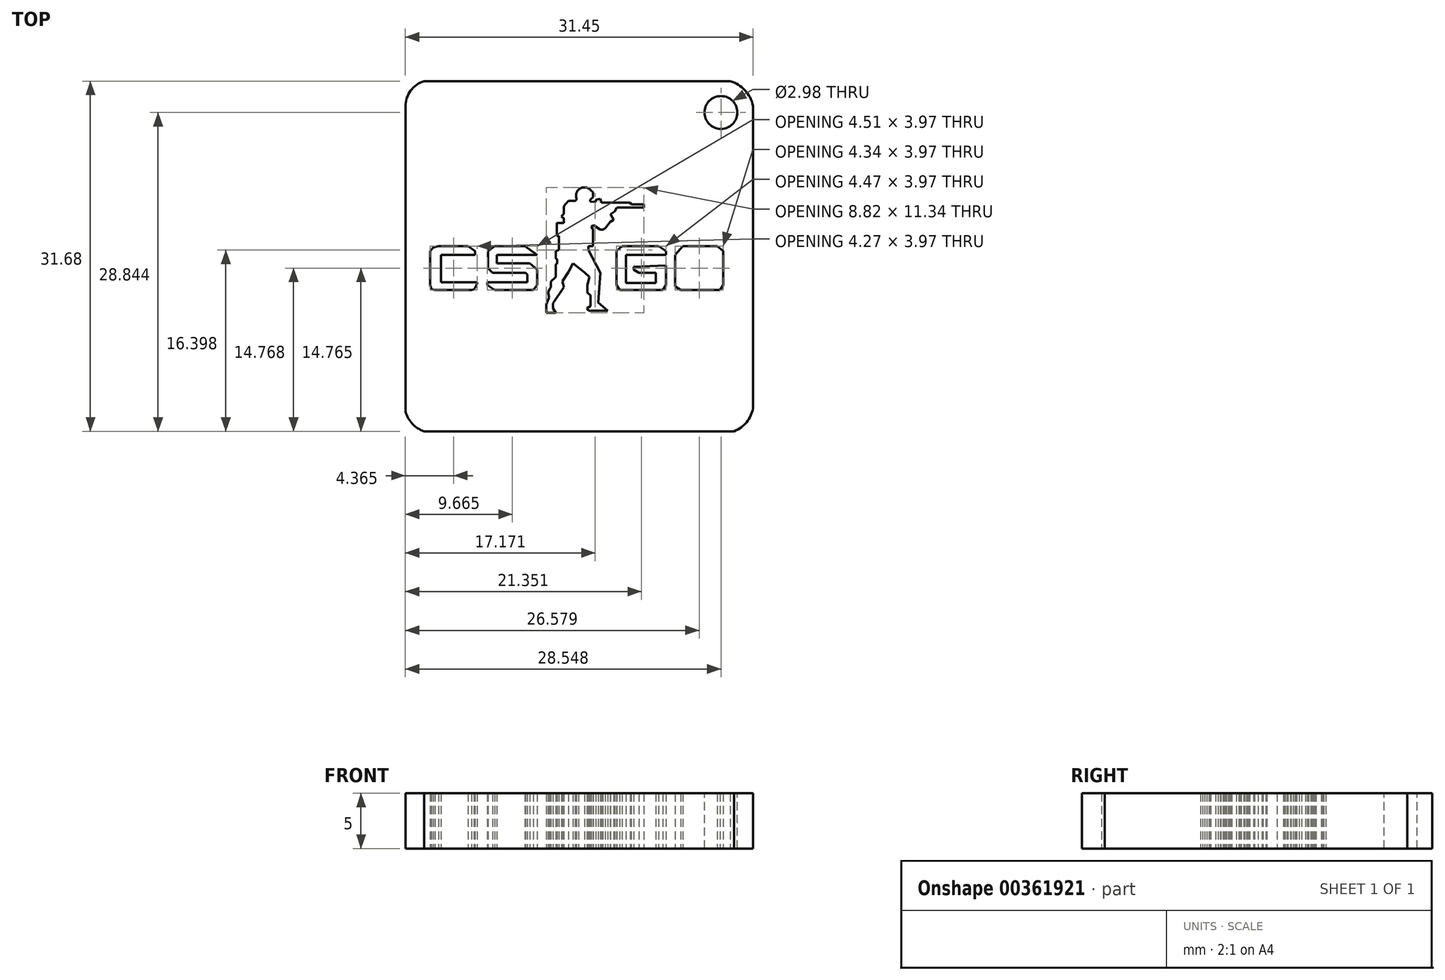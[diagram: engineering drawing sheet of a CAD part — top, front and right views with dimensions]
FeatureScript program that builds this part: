
annotation { "Feature Type Name" : "Feature", "Feature Type Description" : "" }
export const myFeature = defineFeature(function(context is Context, id is Id, definition is map)
    precondition{}
    {
        {
            var Q0;
            Q0=qCreatedBy(makeId("Top.planeOp"),FACE);
            var sketch = newSketch(context, id + "F0", { "sketchPlane" : qUnion([Q0])});
            skLineSegment(sketch, "E0", {"start": v(-16.2, 13.42) * mm, "end": v(-16.2, -14.16) * mm});
            skArc(sketch, "E1", {"start": v(-16.2, -14.16) * mm, "mid": v(-15.58, -15.27) * mm, "end": v(-14.52, -15.96) * mm});
            skLineSegment(sketch, "E2", {"start": v(-14.52, -15.96) * mm, "end": v(13.54, -15.96) * mm});
            skArc(sketch, "E3", {"start": v(13.54, -15.96) * mm, "mid": v(14.66, -15.14) * mm, "end": v(15.25, -13.88) * mm});
            skLineSegment(sketch, "E4", {"start": v(15.25, -13.88) * mm, "end": v(15.25, 13.5) * mm});
            skArc(sketch, "E5", {"start": v(15.25, 13.5) * mm, "mid": v(14.53, 14.89) * mm, "end": v(13.2, 15.72) * mm});
            skLineSegment(sketch, "E6", {"start": v(13.2, 15.72) * mm, "end": v(-14.5, 15.72) * mm});
            skArc(sketch, "E7", {"start": v(-14.5, 15.72) * mm, "mid": v(-15.73, 14.85) * mm, "end": v(-16.2, 13.42) * mm});
            skLineSegment(sketch, "E8", {"start": v(-12.75, 0) * mm, "end": v(-9.89, 0) * mm});
            skLineSegment(sketch, "E9", {"start": v(-9.89, 0) * mm, "end": v(-9.89, 0.36) * mm});
            skLineSegment(sketch, "E10", {"start": v(-9.89, 0.36) * mm, "end": v(-10.53, 0.8) * mm});
            skLineSegment(sketch, "E11", {"start": v(-10.53, 0.8) * mm, "end": v(-13.2, 0.8) * mm});
            skLineSegment(sketch, "E12", {"start": v(-13.2, 0.8) * mm, "end": v(-13.66, 0.67) * mm});
            skLineSegment(sketch, "E13", {"start": v(-13.66, 0.67) * mm, "end": v(-13.97, 0.36) * mm});
            skLineSegment(sketch, "E14", {"start": v(-13.97, 0.36) * mm, "end": v(-13.97, -2.73) * mm});
            skLineSegment(sketch, "E15", {"start": v(-13.97, -2.73) * mm, "end": v(-13.82, -3.11) * mm});
            skLineSegment(sketch, "E16", {"start": v(-13.82, -3.11) * mm, "end": v(-13.52, -3.18) * mm});
            skLineSegment(sketch, "E17", {"start": v(-13.52, -3.18) * mm, "end": v(-10.21, -3.18) * mm});
            skLineSegment(sketch, "E18", {"start": v(-10.21, -3.18) * mm, "end": v(-9.99, -3.11) * mm});
            skLineSegment(sketch, "E19", {"start": v(-9.99, -3.11) * mm, "end": v(-9.89, -3) * mm});
            skLineSegment(sketch, "E20", {"start": v(-9.89, -3) * mm, "end": v(-9.7, -2.6) * mm});
            skLineSegment(sketch, "E21", {"start": v(-9.7, -2.6) * mm, "end": v(-9.7, -2.47) * mm});
            skLineSegment(sketch, "E22", {"start": v(-9.7, -2.47) * mm, "end": v(-12.97, -2.47) * mm});
            skLineSegment(sketch, "E23", {"start": v(-12.97, -2.47) * mm, "end": v(-12.97, -0.32) * mm});
            skLineSegment(sketch, "E24", {"start": v(-12.97, -0.32) * mm, "end": v(-12.97, 0) * mm});
            skLineSegment(sketch, "E25", {"start": v(-12.97, 0) * mm, "end": v(-12.75, 0) * mm});
            skLineSegment(sketch, "E26", {"start": v(-8.11, 0.8) * mm, "end": v(-5.38, 0.8) * mm});
            skLineSegment(sketch, "E27", {"start": v(-5.38, 0.8) * mm, "end": v(-4.28, 0) * mm});
            skLineSegment(sketch, "E28", {"start": v(-4.28, 0) * mm, "end": v(-7.92, 0) * mm});
            skLineSegment(sketch, "E29", {"start": v(-7.92, 0) * mm, "end": v(-7.92, -0.77) * mm});
            skLineSegment(sketch, "E30", {"start": v(-7.92, -0.77) * mm, "end": v(-4.94, -0.77) * mm});
            skLineSegment(sketch, "E31", {"start": v(-4.94, -0.77) * mm, "end": v(-4.28, -1.33) * mm});
            skLineSegment(sketch, "E32", {"start": v(-4.28, -1.33) * mm, "end": v(-4.28, -2.73) * mm});
            skLineSegment(sketch, "E33", {"start": v(-4.28, -2.73) * mm, "end": v(-4.61, -3.18) * mm});
            skLineSegment(sketch, "E34", {"start": v(-4.61, -3.18) * mm, "end": v(-8.13, -3.18) * mm});
            skLineSegment(sketch, "E35", {"start": v(-8.13, -3.18) * mm, "end": v(-8.79, -2.73) * mm});
            skLineSegment(sketch, "E36", {"start": v(-8.79, -2.73) * mm, "end": v(-8.79, -2.47) * mm});
            skLineSegment(sketch, "E37", {"start": v(-8.79, -2.47) * mm, "end": v(-5.15, -2.47) * mm});
            skLineSegment(sketch, "E38", {"start": v(-5.15, -2.47) * mm, "end": v(-5.15, -1.76) * mm});
            skLineSegment(sketch, "E39", {"start": v(-5.15, -1.76) * mm, "end": v(-5.32, -1.6) * mm});
            skLineSegment(sketch, "E40", {"start": v(-5.32, -1.6) * mm, "end": v(-8.3, -1.6) * mm});
            skLineSegment(sketch, "E41", {"start": v(-8.3, -1.6) * mm, "end": v(-8.72, -1.2) * mm});
            skLineSegment(sketch, "E42", {"start": v(-8.72, -1.2) * mm, "end": v(-8.72, 0) * mm});
            skLineSegment(sketch, "E43", {"start": v(-8.72, 0) * mm, "end": v(-8.72, 0.36) * mm});
            skLineSegment(sketch, "E44", {"start": v(-8.72, 0.36) * mm, "end": v(-8.11, 0.8) * mm});
            skLineSegment(sketch, "E45", {"start": v(0.51, 4.82) * mm, "end": v(0.51, 5) * mm});
            skLineSegment(sketch, "E46", {"start": v(0.63, 5.08) * mm, "end": v(0.51, 5) * mm});
            skLineSegment(sketch, "E47", {"start": v(0.63, 5.08) * mm, "end": v(0.77, 5.21) * mm});
            skLineSegment(sketch, "E48", {"start": v(0.77, 5.21) * mm, "end": v(0.77, 5.36) * mm});
            skLineSegment(sketch, "E49", {"start": v(0.77, 5.36) * mm, "end": v(0.77, 5.53) * mm});
            skLineSegment(sketch, "E50", {"start": v(0.77, 5.53) * mm, "end": v(0.77, 5.7) * mm});
            skLineSegment(sketch, "E51", {"start": v(0.77, 5.7) * mm, "end": v(0.63, 5.81) * mm});
            skLineSegment(sketch, "E52", {"start": v(0.63, 5.81) * mm, "end": v(0.51, 5.91) * mm});
            skArc(sketch, "E53", {"start": v(0.51, 5.91) * mm, "mid": v(-0.01, 6.1) * mm, "end": v(-0.53, 5.91) * mm});
            skArc(sketch, "E54", {"start": v(-0.53, 5.91) * mm, "mid": v(-0.75, 5.53) * mm, "end": v(-0.71, 5.1) * mm});
            skArc(sketch, "E55", {"start": v(-0.84, 4.9) * mm, "mid": v(-0.74, 4.97) * mm, "end": v(-0.71, 5.1) * mm});
            skLineSegment(sketch, "E56", {"start": v(-0.84, 4.9) * mm, "end": v(-1.45, 4.9) * mm});
            skLineSegment(sketch, "E57", {"start": v(-1.45, 4.9) * mm, "end": v(-1.86, 4.42) * mm});
            skLineSegment(sketch, "E58", {"start": v(-1.86, 4.42) * mm, "end": v(-1.86, 3.7) * mm});
            skLineSegment(sketch, "E59", {"start": v(-1.86, 3.7) * mm, "end": v(-2.1, 3.5) * mm});
            skLineSegment(sketch, "E60", {"start": v(-2.1, 3.5) * mm, "end": v(-2, 3.39) * mm});
            skLineSegment(sketch, "E61", {"start": v(-2, 3.39) * mm, "end": v(-1.86, 3.32) * mm});
            skLineSegment(sketch, "E62", {"start": v(-1.86, 3.32) * mm, "end": v(-1.86, 2.9) * mm});
            skLineSegment(sketch, "E63", {"start": v(-1.86, 2.9) * mm, "end": v(-2.5, 2.9) * mm});
            skLineSegment(sketch, "E64", {"start": v(-2.5, 2.9) * mm, "end": v(-2.5, 1.71) * mm});
            skLineSegment(sketch, "E65", {"start": v(-2.5, 1.71) * mm, "end": v(-2.3, 1.71) * mm});
            skLineSegment(sketch, "E66", {"start": v(-2.3, 1.71) * mm, "end": v(-2.3, 0.43) * mm});
            skLineSegment(sketch, "E67", {"start": v(-2.3, 0.43) * mm, "end": v(-2.6, 0.34) * mm});
            skLineSegment(sketch, "E68", {"start": v(-2.6, 0.34) * mm, "end": v(-2.6, -0.32) * mm});
            skLineSegment(sketch, "E69", {"start": v(-2.6, -0.32) * mm, "end": v(-2.46, -0.42) * mm});
            skLineSegment(sketch, "E70", {"start": v(-2.46, -0.42) * mm, "end": v(-2.46, -0.77) * mm});
            skLineSegment(sketch, "E71", {"start": v(-2.46, -0.77) * mm, "end": v(-2.6, -0.87) * mm});
            skLineSegment(sketch, "E72", {"start": v(-2.6, -0.87) * mm, "end": v(-2.6, -2) * mm});
            skLineSegment(sketch, "E73", {"start": v(-2.6, -2) * mm, "end": v(-3.03, -2.4) * mm});
            skLineSegment(sketch, "E74", {"start": v(-3.03, -2.4) * mm, "end": v(-3.03, -2.88) * mm});
            skLineSegment(sketch, "E75", {"start": v(-3.03, -2.88) * mm, "end": v(-3.14, -3.07) * mm});
            skLineSegment(sketch, "E76", {"start": v(-3.14, -3.07) * mm, "end": v(-3.3, -3.37) * mm});
            skLineSegment(sketch, "E77", {"start": v(-3.3, -3.37) * mm, "end": v(-3.2, -3.84) * mm});
            skLineSegment(sketch, "E78", {"start": v(-3.2, -3.84) * mm, "end": v(-3.44, -4.47) * mm});
            skLineSegment(sketch, "E79", {"start": v(-3.44, -4.47) * mm, "end": v(-3.44, -4.87) * mm});
            skLineSegment(sketch, "E80", {"start": v(-3.44, -4.87) * mm, "end": v(-3.44, -5.23) * mm});
            skLineSegment(sketch, "E81", {"start": v(-3.44, -5.23) * mm, "end": v(-2.6, -5.23) * mm});
            skLineSegment(sketch, "E82", {"start": v(-2.6, -5.23) * mm, "end": v(-2.85, -4.83) * mm});
            skLineSegment(sketch, "E83", {"start": v(-2.85, -4.83) * mm, "end": v(-2.85, -4.38) * mm});
            skLineSegment(sketch, "E84", {"start": v(-2.85, -4.38) * mm, "end": v(-1.86, -2.91) * mm});
            skLineSegment(sketch, "E85", {"start": v(-1.86, -2.91) * mm, "end": v(-2, -2.39) * mm});
            skLineSegment(sketch, "E86", {"start": v(-2, -2.39) * mm, "end": v(-1.45, -1.55) * mm});
            skLineSegment(sketch, "E87", {"start": v(-1.45, -1.55) * mm, "end": v(-1.03, -0.77) * mm});
            skLineSegment(sketch, "E88", {"start": v(-1.03, -0.77) * mm, "end": v(0, -1.59) * mm});
            skLineSegment(sketch, "E89", {"start": v(0, -1.59) * mm, "end": v(0.46, -2) * mm});
            skLineSegment(sketch, "E90", {"start": v(0.46, -2) * mm, "end": v(0.27, -2.73) * mm});
            skLineSegment(sketch, "E91", {"start": v(0.27, -2.73) * mm, "end": v(0.27, -3.44) * mm});
            skLineSegment(sketch, "E92", {"start": v(0.27, -3.44) * mm, "end": v(0.54, -3.64) * mm});
            skLineSegment(sketch, "E93", {"start": v(0.54, -3.64) * mm, "end": v(0.54, -4.65) * mm});
            skLineSegment(sketch, "E94", {"start": v(0.54, -4.65) * mm, "end": v(0.24, -4.83) * mm});
            skLineSegment(sketch, "E95", {"start": v(0.24, -4.83) * mm, "end": v(0.37, -5.04) * mm});
            skLineSegment(sketch, "E96", {"start": v(0.37, -5.04) * mm, "end": v(2.12, -5.04) * mm});
            skLineSegment(sketch, "E97", {"start": v(2.12, -5.04) * mm, "end": v(1.23, -4.3) * mm});
            skLineSegment(sketch, "E98", {"start": v(1.23, -4.3) * mm, "end": v(1.44, -1.63) * mm});
            skLineSegment(sketch, "E99", {"start": v(1.44, -1.63) * mm, "end": v(0.35, 0.43) * mm});
            skLineSegment(sketch, "E100", {"start": v(0.35, 0.43) * mm, "end": v(0.35, 0.8) * mm});
            skLineSegment(sketch, "E101", {"start": v(0.35, 0.8) * mm, "end": v(0.78, 0.8) * mm});
            skLineSegment(sketch, "E102", {"start": v(0.78, 0.8) * mm, "end": v(0.78, 2.32) * mm});
            skLineSegment(sketch, "E103", {"start": v(0.78, 2.32) * mm, "end": v(0.63, 2.58) * mm});
            skLineSegment(sketch, "E104", {"start": v(0.63, 2.58) * mm, "end": v(0.81, 2.7) * mm});
            skLineSegment(sketch, "E105", {"start": v(0.81, 2.7) * mm, "end": v(1.44, 2.28) * mm});
            skLineSegment(sketch, "E106", {"start": v(1.44, 2.28) * mm, "end": v(1.65, 2.28) * mm});
            skLineSegment(sketch, "E107", {"start": v(1.65, 2.28) * mm, "end": v(1.88, 2.42) * mm});
            skLineSegment(sketch, "E108", {"start": v(1.88, 2.42) * mm, "end": v(2.33, 2.98) * mm});
            skLineSegment(sketch, "E109", {"start": v(2.33, 2.98) * mm, "end": v(2.5, 3.08) * mm});
            skLineSegment(sketch, "E110", {"start": v(2.5, 3.08) * mm, "end": v(2.66, 3.18) * mm});
            skLineSegment(sketch, "E111", {"start": v(2.66, 3.18) * mm, "end": v(2.56, 3.34) * mm});
            skLineSegment(sketch, "E112", {"start": v(2.56, 3.34) * mm, "end": v(2.35, 3.7) * mm});
            skLineSegment(sketch, "E113", {"start": v(2.35, 3.7) * mm, "end": v(2.74, 3.94) * mm});
            skLineSegment(sketch, "E114", {"start": v(2.74, 3.94) * mm, "end": v(2.94, 4.27) * mm});
            skLineSegment(sketch, "E115", {"start": v(2.94, 4.27) * mm, "end": v(4.28, 4.27) * mm});
            skLineSegment(sketch, "E116", {"start": v(4.28, 4.27) * mm, "end": v(5.38, 4.27) * mm});
            skLineSegment(sketch, "E117", {"start": v(5.38, 4.27) * mm, "end": v(5.38, 4.57) * mm});
            skLineSegment(sketch, "E118", {"start": v(5.38, 4.57) * mm, "end": v(4.24, 4.57) * mm});
            skLineSegment(sketch, "E119", {"start": v(4.24, 4.57) * mm, "end": v(4.14, 4.74) * mm});
            skLineSegment(sketch, "E120", {"start": v(4.14, 4.74) * mm, "end": v(1.55, 4.74) * mm});
            skLineSegment(sketch, "E121", {"start": v(1.55, 4.74) * mm, "end": v(1.44, 5.1) * mm});
            skLineSegment(sketch, "E122", {"start": v(1.44, 5.1) * mm, "end": v(1.03, 4.97) * mm});
            skLineSegment(sketch, "E123", {"start": v(1.03, 4.97) * mm, "end": v(1.03, 4.78) * mm});
            skLineSegment(sketch, "E124", {"start": v(1.03, 4.78) * mm, "end": v(0.51, 4.82) * mm});
            skLineSegment(sketch, "E125", {"start": v(1.82, 4.1) * mm, "end": v(1.68, 3.83) * mm});
            skLineSegment(sketch, "E126", {"start": v(1.68, 3.83) * mm, "end": v(1.44, 3.77) * mm});
            skLineSegment(sketch, "E127", {"start": v(1.44, 3.77) * mm, "end": v(1.52, 3.63) * mm});
            skLineSegment(sketch, "E128", {"start": v(1.52, 3.63) * mm, "end": v(1.8, 3.63) * mm});
            skLineSegment(sketch, "E129", {"start": v(1.8, 3.63) * mm, "end": v(1.82, 4.1) * mm});
            skLineSegment(sketch, "E130", {"start": v(4.46, -1.07) * mm, "end": v(4.46, -1.33) * mm});
            skLineSegment(sketch, "E131", {"start": v(4.46, -1.33) * mm, "end": v(4.94, -1.63) * mm});
            skLineSegment(sketch, "E132", {"start": v(4.94, -1.63) * mm, "end": v(6.45, -1.63) * mm});
            skLineSegment(sketch, "E133", {"start": v(6.45, -1.63) * mm, "end": v(6.45, -2.53) * mm});
            skLineSegment(sketch, "E134", {"start": v(6.45, -2.53) * mm, "end": v(3.77, -2.53) * mm});
            skLineSegment(sketch, "E135", {"start": v(3.77, -2.53) * mm, "end": v(3.77, 0) * mm});
            skLineSegment(sketch, "E136", {"start": v(3.77, 0) * mm, "end": v(7.39, 0) * mm});
            skLineSegment(sketch, "E137", {"start": v(7.39, 0) * mm, "end": v(7.39, 0.34) * mm});
            skLineSegment(sketch, "E138", {"start": v(7.39, 0.34) * mm, "end": v(6.7, 0.8) * mm});
            skLineSegment(sketch, "E139", {"start": v(6.7, 0.8) * mm, "end": v(3.42, 0.8) * mm});
            skLineSegment(sketch, "E140", {"start": v(3.42, 0.8) * mm, "end": v(2.91, 0.34) * mm});
            skLineSegment(sketch, "E141", {"start": v(2.91, 0.34) * mm, "end": v(2.91, -2.73) * mm});
            skLineSegment(sketch, "E142", {"start": v(2.91, -2.73) * mm, "end": v(3.19, -3.18) * mm});
            skLineSegment(sketch, "E143", {"start": v(3.19, -3.18) * mm, "end": v(7.08, -3.18) * mm});
            skLineSegment(sketch, "E144", {"start": v(7.08, -3.18) * mm, "end": v(7.36, -2.73) * mm});
            skLineSegment(sketch, "E145", {"start": v(7.36, -2.73) * mm, "end": v(7.36, -0.97) * mm});
            skLineSegment(sketch, "E146", {"start": v(7.36, -0.97) * mm, "end": v(4.46, -1.07) * mm});
            skLineSegment(sketch, "E147", {"start": v(12, 0.8) * mm, "end": v(8.9, 0.8) * mm});
            skLineSegment(sketch, "E148", {"start": v(8.9, 0.8) * mm, "end": v(8.2, 0) * mm});
            skLineSegment(sketch, "E149", {"start": v(8.2, 0) * mm, "end": v(8.2, -2.86) * mm});
            skLineSegment(sketch, "E150", {"start": v(8.2, -2.86) * mm, "end": v(8.7, -3.18) * mm});
            skLineSegment(sketch, "E151", {"start": v(8.7, -3.18) * mm, "end": v(12.26, -3.18) * mm});
            skLineSegment(sketch, "E152", {"start": v(12.26, -3.18) * mm, "end": v(12.55, -2.73) * mm});
            skLineSegment(sketch, "E153", {"start": v(12.55, -2.73) * mm, "end": v(12.55, 0.34) * mm});
            skLineSegment(sketch, "E154", {"start": v(12.55, 0.34) * mm, "end": v(12, 0.8) * mm});
            skLineSegment(sketch, "E155", {"start": v(9.15, 0) * mm, "end": v(11.72, 0) * mm});
            skLineSegment(sketch, "E156", {"start": v(11.72, 0) * mm, "end": v(11.72, -2.57) * mm});
            skLineSegment(sketch, "E157", {"start": v(11.72, -2.57) * mm, "end": v(9.15, -2.57) * mm});
            skLineSegment(sketch, "E158", {"start": v(9.15, -2.57) * mm, "end": v(9.15, 0) * mm});
            skSolve(sketch);
        }
        {
            var Q0;
            Q0 = qSketchRegion(id + "F0", true);
            extrude(context, id + "F1", {"entities" : qUnion([Q0]), "depth" : 5 * mm});
        }
        {
            var Q0;
            Q0=makeQuery(id+"F1.opExtrude","CAP_FACE",FACE,{"disambiguationData":[OSD([sQuery(id+"F0.wireOp",EDGE,"E0"),sQuery(id+"F0.wireOp",EDGE,"E1"),sQuery(id+"F0.wireOp",EDGE,"E2"),sQuery(id+"F0.wireOp",EDGE,"E3"),sQuery(id+"F0.wireOp",EDGE,"E4"),sQuery(id+"F0.wireOp",EDGE,"E5"),sQuery(id+"F0.wireOp",EDGE,"E6"),sQuery(id+"F0.wireOp",EDGE,"E7"),sQuery(id+"F0.wireOp",EDGE,"E8"),sQuery(id+"F0.wireOp",EDGE,"E9"),sQuery(id+"F0.wireOp",EDGE,"E10"),sQuery(id+"F0.wireOp",EDGE,"E11"),sQuery(id+"F0.wireOp",EDGE,"E12"),sQuery(id+"F0.wireOp",EDGE,"E13"),sQuery(id+"F0.wireOp",EDGE,"E14"),sQuery(id+"F0.wireOp",EDGE,"E15"),sQuery(id+"F0.wireOp",EDGE,"E16"),sQuery(id+"F0.wireOp",EDGE,"E17"),sQuery(id+"F0.wireOp",EDGE,"E18"),sQuery(id+"F0.wireOp",EDGE,"E19"),sQuery(id+"F0.wireOp",EDGE,"E20"),sQuery(id+"F0.wireOp",EDGE,"E21"),sQuery(id+"F0.wireOp",EDGE,"E22"),sQuery(id+"F0.wireOp",EDGE,"E23"),sQuery(id+"F0.wireOp",EDGE,"E24"),sQuery(id+"F0.wireOp",EDGE,"E25"),sQuery(id+"F0.wireOp",EDGE,"E26"),sQuery(id+"F0.wireOp",EDGE,"E27"),sQuery(id+"F0.wireOp",EDGE,"E28"),sQuery(id+"F0.wireOp",EDGE,"E29"),sQuery(id+"F0.wireOp",EDGE,"E30"),sQuery(id+"F0.wireOp",EDGE,"E31"),sQuery(id+"F0.wireOp",EDGE,"E32"),sQuery(id+"F0.wireOp",EDGE,"E33"),sQuery(id+"F0.wireOp",EDGE,"E34"),sQuery(id+"F0.wireOp",EDGE,"E35"),sQuery(id+"F0.wireOp",EDGE,"E36"),sQuery(id+"F0.wireOp",EDGE,"E37"),sQuery(id+"F0.wireOp",EDGE,"E38"),sQuery(id+"F0.wireOp",EDGE,"E39"),sQuery(id+"F0.wireOp",EDGE,"E40"),sQuery(id+"F0.wireOp",EDGE,"E41"),sQuery(id+"F0.wireOp",EDGE,"E42"),sQuery(id+"F0.wireOp",EDGE,"E43"),sQuery(id+"F0.wireOp",EDGE,"E44"),sQuery(id+"F0.wireOp",EDGE,"E45"),sQuery(id+"F0.wireOp",EDGE,"E46"),sQuery(id+"F0.wireOp",EDGE,"E47"),sQuery(id+"F0.wireOp",EDGE,"E48"),sQuery(id+"F0.wireOp",EDGE,"E49"),sQuery(id+"F0.wireOp",EDGE,"E50"),sQuery(id+"F0.wireOp",EDGE,"E51"),sQuery(id+"F0.wireOp",EDGE,"E52"),sQuery(id+"F0.wireOp",EDGE,"E53"),sQuery(id+"F0.wireOp",EDGE,"E54"),sQuery(id+"F0.wireOp",EDGE,"E55"),sQuery(id+"F0.wireOp",EDGE,"E56"),sQuery(id+"F0.wireOp",EDGE,"E57"),sQuery(id+"F0.wireOp",EDGE,"E58"),sQuery(id+"F0.wireOp",EDGE,"E59"),sQuery(id+"F0.wireOp",EDGE,"E60"),sQuery(id+"F0.wireOp",EDGE,"E61"),sQuery(id+"F0.wireOp",EDGE,"E62"),sQuery(id+"F0.wireOp",EDGE,"E63"),sQuery(id+"F0.wireOp",EDGE,"E64"),sQuery(id+"F0.wireOp",EDGE,"E65"),sQuery(id+"F0.wireOp",EDGE,"E66"),sQuery(id+"F0.wireOp",EDGE,"E67"),sQuery(id+"F0.wireOp",EDGE,"E68"),sQuery(id+"F0.wireOp",EDGE,"E69"),sQuery(id+"F0.wireOp",EDGE,"E70"),sQuery(id+"F0.wireOp",EDGE,"E71"),sQuery(id+"F0.wireOp",EDGE,"E72"),sQuery(id+"F0.wireOp",EDGE,"E73"),sQuery(id+"F0.wireOp",EDGE,"E74"),sQuery(id+"F0.wireOp",EDGE,"E75"),sQuery(id+"F0.wireOp",EDGE,"E76"),sQuery(id+"F0.wireOp",EDGE,"E77"),sQuery(id+"F0.wireOp",EDGE,"E78"),sQuery(id+"F0.wireOp",EDGE,"E79"),sQuery(id+"F0.wireOp",EDGE,"E80"),sQuery(id+"F0.wireOp",EDGE,"E81"),sQuery(id+"F0.wireOp",EDGE,"E82"),sQuery(id+"F0.wireOp",EDGE,"E83"),sQuery(id+"F0.wireOp",EDGE,"E84"),sQuery(id+"F0.wireOp",EDGE,"E85"),sQuery(id+"F0.wireOp",EDGE,"E86"),sQuery(id+"F0.wireOp",EDGE,"E87"),sQuery(id+"F0.wireOp",EDGE,"E88"),sQuery(id+"F0.wireOp",EDGE,"E89"),sQuery(id+"F0.wireOp",EDGE,"E90"),sQuery(id+"F0.wireOp",EDGE,"E91"),sQuery(id+"F0.wireOp",EDGE,"E92"),sQuery(id+"F0.wireOp",EDGE,"E93"),sQuery(id+"F0.wireOp",EDGE,"E94"),sQuery(id+"F0.wireOp",EDGE,"E95"),sQuery(id+"F0.wireOp",EDGE,"E96"),sQuery(id+"F0.wireOp",EDGE,"E97"),sQuery(id+"F0.wireOp",EDGE,"E98"),sQuery(id+"F0.wireOp",EDGE,"E99"),sQuery(id+"F0.wireOp",EDGE,"E100"),sQuery(id+"F0.wireOp",EDGE,"E101"),sQuery(id+"F0.wireOp",EDGE,"E102"),sQuery(id+"F0.wireOp",EDGE,"E103"),sQuery(id+"F0.wireOp",EDGE,"E104"),sQuery(id+"F0.wireOp",EDGE,"E105"),sQuery(id+"F0.wireOp",EDGE,"E106"),sQuery(id+"F0.wireOp",EDGE,"E107"),sQuery(id+"F0.wireOp",EDGE,"E108"),sQuery(id+"F0.wireOp",EDGE,"E109"),sQuery(id+"F0.wireOp",EDGE,"E110"),sQuery(id+"F0.wireOp",EDGE,"E111"),sQuery(id+"F0.wireOp",EDGE,"E112"),sQuery(id+"F0.wireOp",EDGE,"E113"),sQuery(id+"F0.wireOp",EDGE,"E114"),sQuery(id+"F0.wireOp",EDGE,"E115"),sQuery(id+"F0.wireOp",EDGE,"E116"),sQuery(id+"F0.wireOp",EDGE,"E117"),sQuery(id+"F0.wireOp",EDGE,"E118"),sQuery(id+"F0.wireOp",EDGE,"E119"),sQuery(id+"F0.wireOp",EDGE,"E120"),sQuery(id+"F0.wireOp",EDGE,"E121"),sQuery(id+"F0.wireOp",EDGE,"E122"),sQuery(id+"F0.wireOp",EDGE,"E123"),sQuery(id+"F0.wireOp",EDGE,"E124"),sQuery(id+"F0.wireOp",EDGE,"E130"),sQuery(id+"F0.wireOp",EDGE,"E131"),sQuery(id+"F0.wireOp",EDGE,"E132"),sQuery(id+"F0.wireOp",EDGE,"E133"),sQuery(id+"F0.wireOp",EDGE,"E134"),sQuery(id+"F0.wireOp",EDGE,"E135"),sQuery(id+"F0.wireOp",EDGE,"E136"),sQuery(id+"F0.wireOp",EDGE,"E137"),sQuery(id+"F0.wireOp",EDGE,"E138"),sQuery(id+"F0.wireOp",EDGE,"E139"),sQuery(id+"F0.wireOp",EDGE,"E140"),sQuery(id+"F0.wireOp",EDGE,"E141"),sQuery(id+"F0.wireOp",EDGE,"E142"),sQuery(id+"F0.wireOp",EDGE,"E143"),sQuery(id+"F0.wireOp",EDGE,"E144"),sQuery(id+"F0.wireOp",EDGE,"E145"),sQuery(id+"F0.wireOp",EDGE,"E146"),sQuery(id+"F0.wireOp",EDGE,"E147"),sQuery(id+"F0.wireOp",EDGE,"E148"),sQuery(id+"F0.wireOp",EDGE,"E149"),sQuery(id+"F0.wireOp",EDGE,"E150"),sQuery(id+"F0.wireOp",EDGE,"E151"),sQuery(id+"F0.wireOp",EDGE,"E152"),sQuery(id+"F0.wireOp",EDGE,"E153"),sQuery(id+"F0.wireOp",EDGE,"E154")])],"isStart":false});
            var sketch = newSketch(context, id + "F2", { "sketchPlane" : qUnion([Q0])});
            skCircle(sketch, "E159", {"center": v(12.35, 12.88) * mm, "radius": 1.49 * mm});
            skSolve(sketch);
        }
        {
            var Q0;
            Q0 = qSketchRegion(id + "F2", true);
            extrude(context, id + "F3", {"entities" : qUnion([Q0]), "operationType" : NewBodyOperationType.REMOVE, "oppositeDirection" : true, "depth" : 25 * mm});
        }
    });
